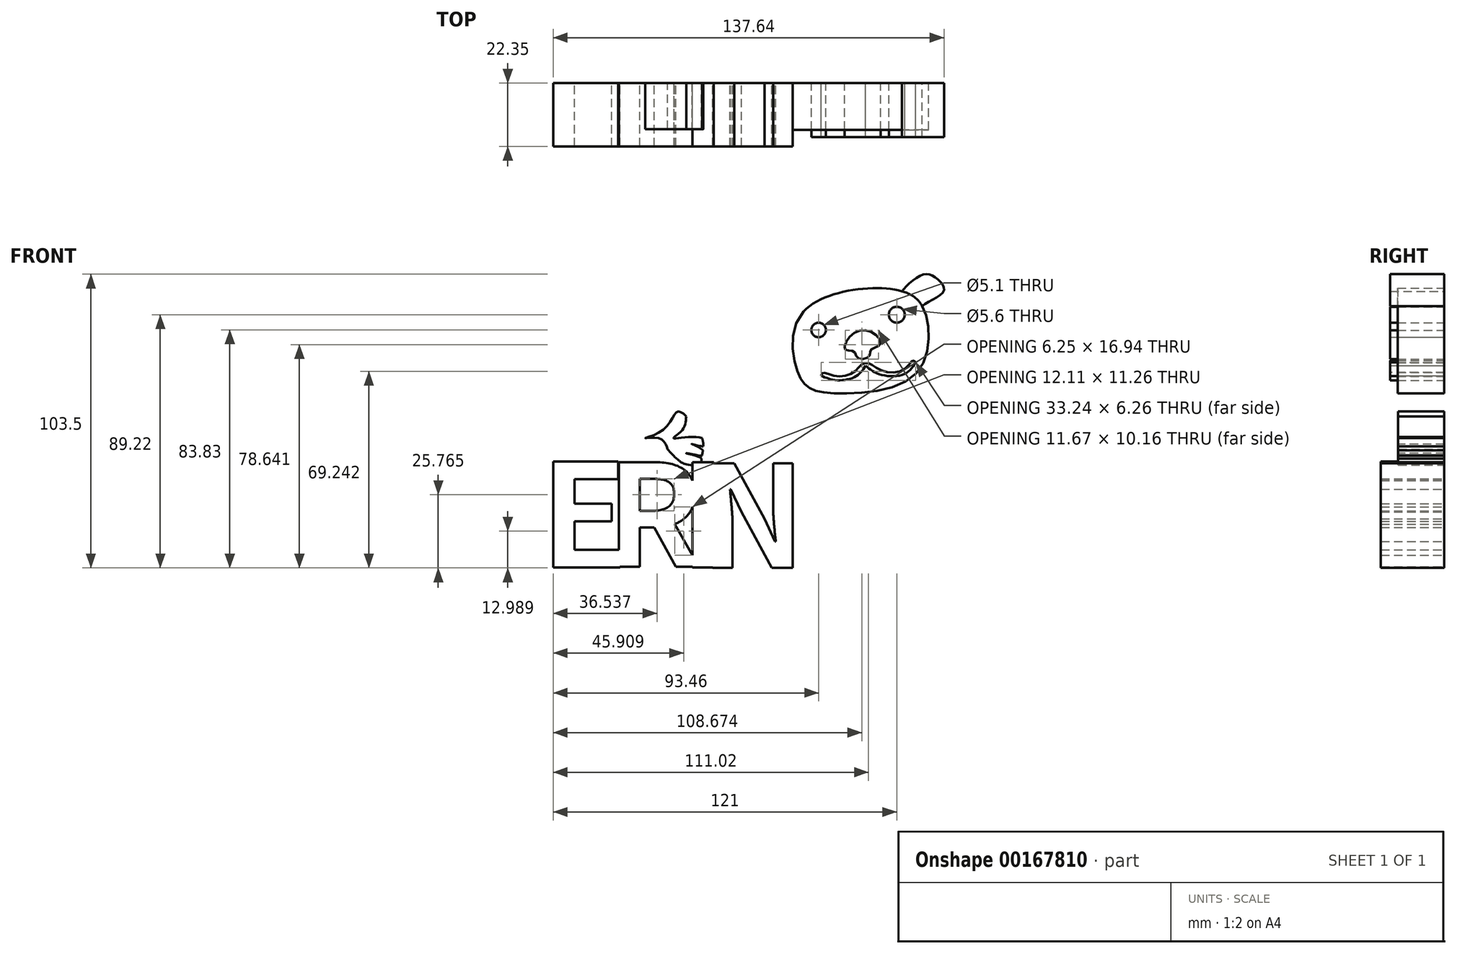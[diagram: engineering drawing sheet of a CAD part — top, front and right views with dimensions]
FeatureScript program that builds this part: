
annotation { "Feature Type Name" : "Feature", "Feature Type Description" : "" }
export const myFeature = defineFeature(function(context is Context, id is Id, definition is map)
    precondition{}
    {
        {
            var Q0;
            Q0=qCreatedBy(makeId("Front.planeOp"),FACE);
            var sketch = newSketch(context, id + "F0", { "sketchPlane" : qUnion([Q0])});
            skFitSpline(sketch, "E0", {"points": [v(58.07, 51.78) * mm, v(23.43, 44.63) * mm, v(21.05, 24.1) * mm, v(25.16, 17.95) * mm, v(34.48, 15.8) * mm, v(62.44, 22.21) * mm, v(66.87, 41.88) * mm, v(58.07, 51.78) * mm]});
            skCircle(sketch, "E1", {"center": v(28.72, 38.13) * mm, "radius": 2.55 * mm});
            skCircle(sketch, "E2", {"center": v(56.26, 43.52) * mm, "radius": 2.8 * mm});
            skFitSpline(sketch, "E3", {"points": [v(23.43, 44.63) * mm, v(13.68, 47.33) * mm, v(10.11, 42.07) * mm, v(11.25, 38.32) * mm, v(20.04, 37.98) * mm], "startDerivative": vector(-29, 14.08) * mm, "endDerivative": vector(20.58, 7.7) * mm});
            skFitSpline(sketch, "E4", {"points": [v(58.07, 51.78) * mm, v(64.96, 57.47) * mm, v(70.22, 56.35) * mm, v(72.74, 51.78) * mm, v(65.23, 46.54) * mm], "startDerivative": vector(10.24, 15.1) * mm, "endDerivative": vector(-17.35, -17.75) * mm});
            skFitSpline(sketch, "E5", {"points": [v(38.1, 31.18) * mm, v(40.18, 36.25) * mm, v(47.31, 37.38) * mm, v(50.5, 33.06) * mm, v(47.12, 31.18) * mm, v(46.56, 28.92) * mm, v(42.62, 28.17) * mm, v(41.11, 30.61) * mm, v(38.1, 31.18) * mm]});
            skFitSpline(sketch, "E6", {"points": [v(45.25, 25.54) * mm, v(50.13, 22.54) * mm, v(58.77, 22.54) * mm, v(62.9, 26.67) * mm], "startDerivative": vector(13.48, -11.2) * mm, "endDerivative": vector(10.45, 15.83) * mm});
            skFitSpline(sketch, "E7", {"points": [v(45.25, 25.54) * mm, v(41.87, 21.79) * mm, v(34.73, 20.47) * mm, v(29.66, 21.97) * mm], "startDerivative": vector(-8.64, -13.66) * mm, "endDerivative": vector(-14.6, 6.2) * mm});
            skFitSpline(sketch, "E8", {"points": [v(20.04, 37.98) * mm, v(3.03, 29.48) * mm, v(-13.35, 38.32) * mm, v(-21.8, 42.21) * mm, v(-42.1, 38.32) * mm, v(-66.5, 0) * mm, v(-78.9, -3.57) * mm, v(-92.05, 4.31) * mm, v(-93.73, 14.47) * mm, v(-98.82, 12.96) * mm, v(-90.92, -6.96) * mm, v(-49.42, -2.81) * mm, v(-34.4, -10.52) * mm, v(-30.96, -10.52) * mm, v(-34.4, -6.75) * mm, v(-30.96, -8.73) * mm, v(-28.94, -9.8) * mm, v(-27.96, -8.44) * mm, v(-30.67, -5.39) * mm, v(-32.91, -3.74) * mm, v(-30.06, -4.7) * mm, v(-26.69, -7.53) * mm, v(-24.62, -5.64) * mm, v(-24.81, -2.81) * mm, v(-27.63, 0) * mm, v(-32.35, 0) * mm, v(-25.6, 3.3) * mm, v(-21.15, 9.31) * mm, v(-17.9, 7.69) * mm, v(-11.94, -1.7) * mm, v(-12.16, -9.76) * mm, v(-1.55, -14.83) * mm, v(2.31, -13.96) * mm, v(0, -12.2) * mm, v(-1.5, -11.58) * mm, v(-3.15, -10.91) * mm, v(0, -11.65) * mm, v(3.71, -13.96) * mm, v(3.71, -9.03) * mm, v(0.54, -7.23) * mm, v(0, -7.07) * mm, v(-0.93, -6.44) * mm, v(1.66, -7.14) * mm, v(4.17, -8.21) * mm, v(6.69, -8.24) * mm, v(4.84, -4.53) * mm, v(0, -3.92) * mm, v(-3.97, -1) * mm, v(0, 5.01) * mm, v(11.25, 0) * mm, v(26.84, 3.2) * mm, v(39.61, 15.75) * mm], "startDerivative": vector(-353.5, -340.22) * mm, "endDerivative": vector(362.9, 476.23) * mm});
            skFitSpline(sketch, "E9", {"points": [v(11.25, 0) * mm, v(11.25, -12.77) * mm, v(24.5, -13.18) * mm, v(18.75, -10.33) * mm, v(18.75, -10.33) * mm, v(21.75, -10.88) * mm, v(25.9, -11.64) * mm, v(25.9, -9.77) * mm, v(24.2, -8.26) * mm, v(18.19, -8.26) * mm, v(20.07, -7.32) * mm, v(25.51, -7.89) * mm, v(27.58, -7.32) * mm, v(27.77, -4.7) * mm, v(23.83, -2.16) * mm, v(15.75, -5.45) * mm, v(16.5, 0) * mm], "startDerivative": vector(-56.25, -155.65) * mm, "endDerivative": vector(88.77, -100.75) * mm});
            skFitSpline(sketch, "E10", {"points": [v(-17.9, 7.69) * mm, v(-19.25, 2.94) * mm, v(-22.33, 0) * mm, v(-12.34, 0) * mm, v(-11.17, -2.68) * mm, v(-15.98, -2.05) * mm, v(-12.04, -4.27) * mm, v(-12.35, -6.04) * mm, v(-15.16, -5.77) * mm, v(-17.9, -5.32) * mm, v(-12.44, -7.22) * mm, v(-13.07, -9.13) * mm, v(-18.8, -8.95) * mm, v(-20.25, -8.04) * mm, v(-21.6, -6.95) * mm, v(-24.5, -3.86) * mm], "startDerivative": vector(-7.12, -62.97) * mm, "endDerivative": vector(-41.79, 47.23) * mm});
            skFitSpline(sketch, "E11", {"points": [v(29.66, 21.97) * mm, v(30.27, 23.08) * mm, v(34.2, 21.97) * mm, v(40.91, 23.16) * mm, v(44.1, 26.15) * mm, v(46.56, 26.31) * mm, v(51.46, 23.6) * mm, v(59.14, 24.46) * mm, v(61.9, 27.35) * mm, v(62.9, 26.67) * mm], "startDerivative": vector(5.55, 23.11) * mm, "endDerivative": vector(15.72, -18.3) * mm});
            skSolve(sketch);
        }
        {
            var Q0;
            Q0=qCreatedBy(makeId("Front.planeOp"),FACE);
            var sketch = newSketch(context, id + "F1", { "sketchPlane" : qUnion([Q0])});
            skText(sketch, "E12", { "text": "E", "fontName": "NotoSansCJKtc-Bold.otf"});
            skText(sketch, "E13", { "text": "R", "fontName": "NotoSansCJKtc-Bold.otf"});
            skText(sketch, "E14", { "text": "I", "fontName": "NotoSansCJKtc-Bold.otf"});
            skText(sketch, "E15", { "text": "N", "fontName": "NotoSansCJKtc-Bold.otf"});
            const initialGuessF1  = {"E12": [-0.06932, -0.04552, 1, 0, 0.03628], "E13": [-0.04617, -0.04535, 1, 0, 0.03588], "E14": [-0.02026, -0.04556, 1, 0, 0.03604], "E15": [-0.0131, -0.0457, 1, 0, 0.03588]};
            skSetInitialGuess(sketch, initialGuessF1);
            skSolve(sketch);
        }
        {
            var Q0;
            Q0=makeQuery(id+"F0.imprint","IMPRINT",FACE,{"disambiguationData":[TD([[makeQuery(id+"F0.imprint","IMPRINT",EDGE,{"derivedFrom":sQuery(id+"F0.wireOp",EDGE,"E5")}),-1.0]])]});
            var Q1;
            {var subQ0=sQuery(id+"F0.wireOp",EDGE,"E3");Q1=makeQuery(id+"F0.imprint","IMPRINT",FACE,{"disambiguationData":[TD([[makeQuery(id+"F0.imprint","IMPRINT",EDGE,{"derivedFrom":subQ0}),1.0]])]});}
            var Q2;
            {var subQ0=sQuery(id+"F0.wireOp",EDGE,"E4");Q2=makeQuery(id+"F0.imprint","IMPRINT",FACE,{"disambiguationData":[TD([[makeQuery(id+"F0.imprint","IMPRINT",EDGE,{"derivedFrom":subQ0}),-1.0]])]});}
            var Q3;
            Q3=makeQuery(id+"F0.imprint","IMPRINT",FACE,{"disambiguationData":[TD([[makeQuery(id+"F0.imprint","IMPRINT",EDGE,{"derivedFrom":sQuery(id+"F0.wireOp",EDGE,"E6")}),1.0]])]});
            var Q4;
            Q4=makeQuery(id+"F0.imprint","IMPRINT",FACE,{"disambiguationData":[TD([[makeQuery(id+"F0.imprint","IMPRINT",EDGE,{"derivedFrom":sQuery(id+"F0.wireOp",EDGE,"E1")}),1.0]])]});
            var Q5;
            Q5=makeQuery(id+"F0.imprint","IMPRINT",FACE,{"disambiguationData":[TD([[makeQuery(id+"F0.imprint","IMPRINT",EDGE,{"derivedFrom":sQuery(id+"F0.wireOp",EDGE,"E2")}),1.0]])]});
            extrude(context, id + "F2", {"entities" : qUnion([Q0, Q1, Q2, Q3, Q4, Q5]), "depth" : 19.05 * mm});
        }
        {
            var Q0;
            {var subQ1=sQuery(id+"F0.wireOp",EDGE,"E8");var subQ9=sQuery(id+"F0.wireOp",EDGE,"E10");var subQ10=makeQuery(id+"F0.imprint","INTERSECT",VERTEX,{"disambiguationData":[OD(0.0)],"derivedFrom":[subQ1,subQ9]});Q0=makeQuery(id+"F0.imprint","IMPRINT",FACE,{"disambiguationData":[TD([[makeQuery(id+"F0.imprint","IMPRINT",EDGE,{"disambiguationData":[TD([[subQ10,1.0]])],"derivedFrom":subQ1}),1.0]])]});}
            var Q1;
            {var subQ4=sQuery(id+"F0.wireOp",EDGE,"E10");Q1=makeQuery(id+"F0.imprint","IMPRINT",FACE,{"disambiguationData":[TD([[makeQuery(id+"F0.imprint","IMPRINT",EDGE,{"derivedFrom":subQ4}),-1.0]])]});}
            var Q2;
            {var subQ0=sQuery(id+"F0.wireOp",EDGE,"E9");var subQ1=sQuery(id+"F0.wireOp",EDGE,"E8");var subQ2=makeQuery(id+"F0.imprint","INTERSECT",VERTEX,{"disambiguationData":[OD(0.0)],"derivedFrom":[subQ1,subQ0]});Q2=makeQuery(id+"F0.imprint","IMPRINT",FACE,{"disambiguationData":[TD([[makeQuery(id+"F0.imprint","IMPRINT",EDGE,{"disambiguationData":[TD([[subQ2,-1.0]])],"derivedFrom":subQ1}),-1.0]])]});}
            extrude(context, id + "F3", {"entities" : qUnion([Q0, Q1, Q2]), "depth" : 16.26 * mm});
        }
        {
            var Q0;
            Q0=makeQuery(id+"F0.imprint","IMPRINT",FACE,{"disambiguationData":[TD([[makeQuery(id+"F0.imprint","IMPRINT",EDGE,{"derivedFrom":sQuery(id+"F0.wireOp",EDGE,"E1")}),-1.0]])]});
            extrude(context, id + "F4", {"entities" : qUnion([Q0]), "depth" : 16.5 * mm});
        }
        {
            var Q0;
            Q0 = qSketchRegion(id + "F1", true);
            extrude(context, id + "F5", {"entities" : qUnion([Q0]), "operationType" : NewBodyOperationType.ADD, "depth" : 22.35 * mm});
        }
    });
